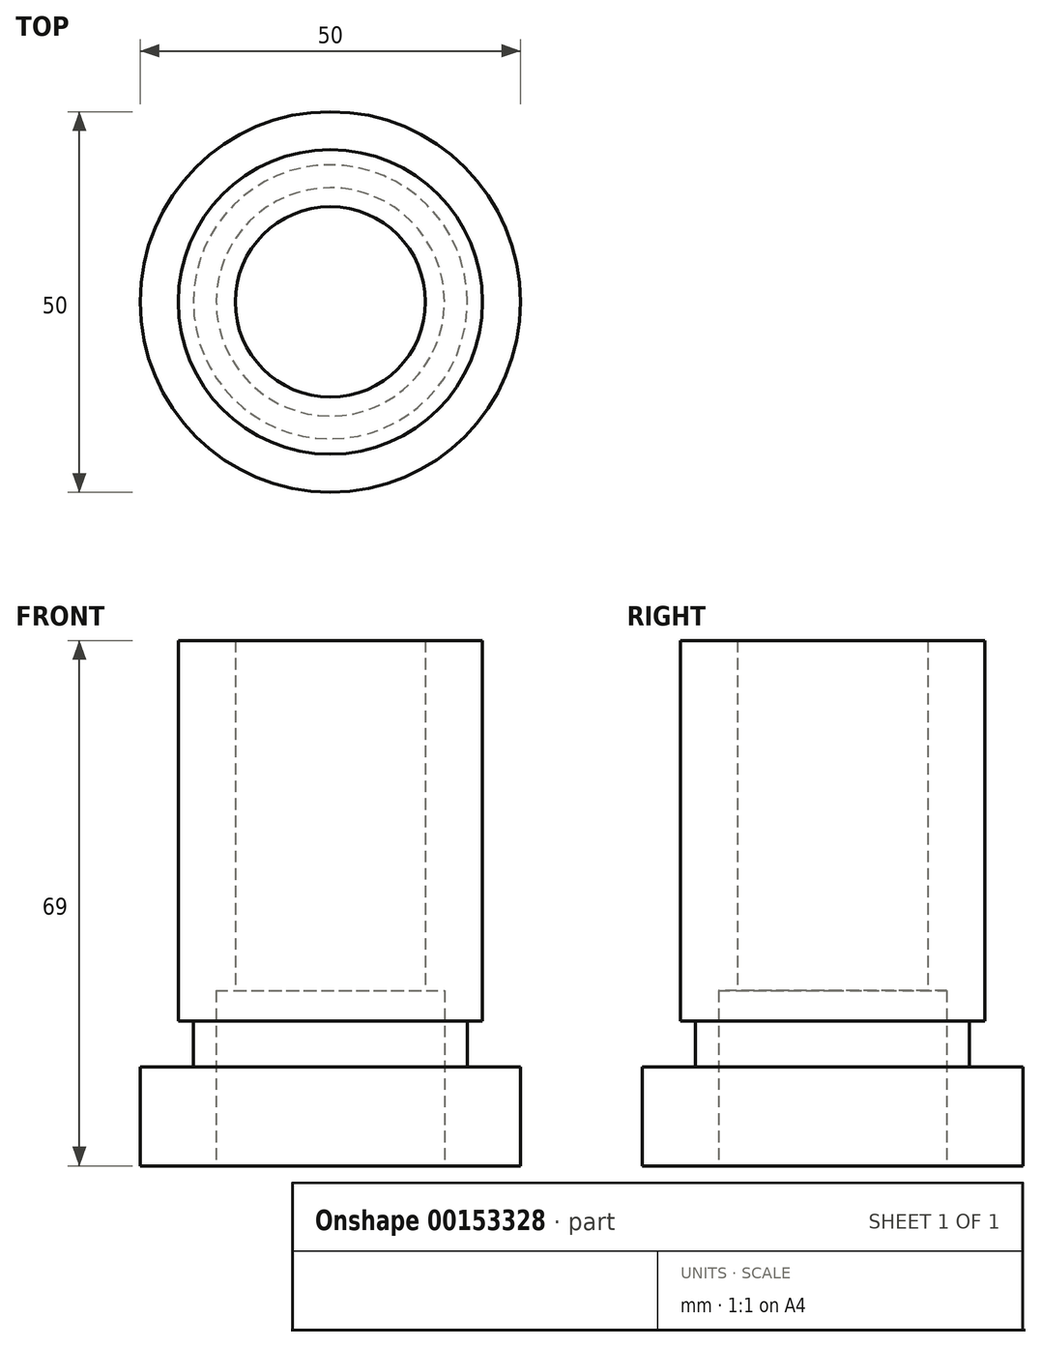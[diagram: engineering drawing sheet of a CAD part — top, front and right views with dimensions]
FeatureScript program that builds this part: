
annotation { "Feature Type Name" : "Feature", "Feature Type Description" : "" }
export const myFeature = defineFeature(function(context is Context, id is Id, definition is map)
    precondition{}
    {
        {
            var Q0;
            Q0=qCreatedBy(makeId("Top.planeOp"),FACE);
            var sketch = newSketch(context, id + "F0", { "sketchPlane" : qUnion([Q0])});
            skCircle(sketch, "E0", {"center": v(0, 0) * mm, "radius": 25 * mm});
            skSolve(sketch);
        }
        {
            var Q0;
            Q0=makeQuery(id+"F0.imprint","IMPRINT",FACE,{"disambiguationData":[TD([[makeQuery(id+"F0.imprint","IMPRINT",EDGE,{"derivedFrom":sQuery(id+"F0.wireOp",EDGE,"E0")}),1.0]])]});
            extrude(context, id + "F1", {"entities" : qUnion([Q0]), "depth" : 13 * mm});
        }
        {
            var Q0;
            Q0=makeQuery(id+"F1.opExtrude","CAP_FACE",FACE,{"disambiguationData":[OSD([sQuery(id+"F0.wireOp",EDGE,"E0")])],"isStart":false});
            var sketch = newSketch(context, id + "F2", { "sketchPlane" : qUnion([Q0])});
            skCircle(sketch, "E1", {"center": v(0, 0) * mm, "radius": 18 * mm});
            skSolve(sketch);
        }
        {
            var Q0;
            Q0=makeQuery(id+"F2.imprint","IMPRINT",FACE,{"disambiguationData":[TD([[makeQuery(id+"F2.imprint","IMPRINT",EDGE,{"derivedFrom":sQuery(id+"F2.wireOp",EDGE,"E1")}),1.0]])]});
            extrude(context, id + "F3", {"entities" : qUnion([Q0]), "operationType" : NewBodyOperationType.ADD, "depth" : 6 * mm});
        }
        {
            var Q0;
            Q0=makeQuery(id+"F3.opExtrude","CAP_FACE",FACE,{"disambiguationData":[OSD([sQuery(id+"F2.wireOp",EDGE,"E1")])],"isStart":false});
            var sketch = newSketch(context, id + "F4", { "sketchPlane" : qUnion([Q0])});
            skCircle(sketch, "E2", {"center": v(0, 0) * mm, "radius": 20 * mm});
            skSolve(sketch);
        }
        {
            var Q0;
            Q0=makeQuery(id+"F4.imprint","IMPRINT",FACE,{"disambiguationData":[TD([[makeQuery(id+"F4.imprint","IMPRINT",EDGE,{"derivedFrom":sQuery(id+"F4.wireOp",EDGE,"E2")}),1.0]])]});
            var Q1;
            Q1=makeQuery(id+"F4.imprint","IMPRINT",FACE,{"disambiguationData":[TD([[makeQuery(id+"F4.imprint","IMPRINT",EDGE,{"derivedFrom":makeQuery(id+"F3.opExtrude","CAP_EDGE",EDGE,{"disambiguationData":[OSD([sQuery(id+"F2.wireOp",EDGE,"E1")])],"isStart":false})}),1.0]])]});
            extrude(context, id + "F5", {"entities" : qUnion([Q0, Q1]), "operationType" : NewBodyOperationType.ADD, "depth" : 50 * mm});
        }
        {
            var Q0;
            Q0=makeQuery(id+"F1.opExtrude","CAP_FACE",FACE,{"disambiguationData":[OSD([sQuery(id+"F0.wireOp",EDGE,"E0")])],"isStart":true});
            var sketch = newSketch(context, id + "F6", { "sketchPlane" : qUnion([Q0])});
            skPoint(sketch, "E3", {"position": v(0, 0) * mm});
            skSolve(sketch);
        }
        {
            var Q0;
            Q0=sQuery(id+"F6.wireOp",VERTEX,"E3");
            var Q1;
            Q1=makeQuery(id+"F1.opExtrude","SWEPT_BODY",BODY,{"disambiguationData":[OSD([sQuery(id+"F0.wireOp",EDGE,"E0")])]});
            hole(context, id + "F7", {"style" : HoleStyle.C_BORE, "endStyle" : HoleEndStyle.THROUGH, "holeDiameter" : 25 * mm, "cBoreDiameter" : 30 * mm, "cBoreDepth" : 23 * mm, "startFromSketch" : true, "locations" : qUnion([Q0]), "scope" : qUnion([Q1]), "isTappedThrough" : true});
        }
    });
